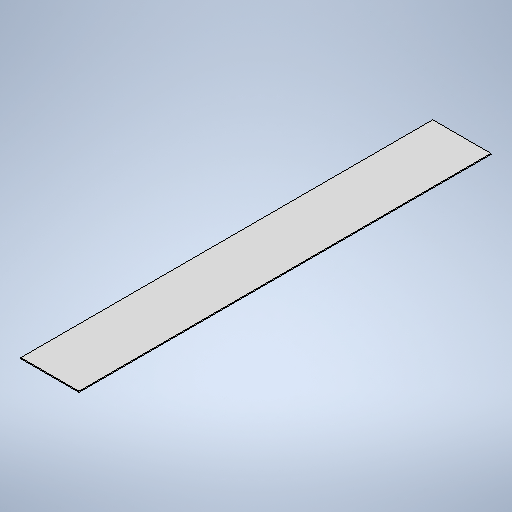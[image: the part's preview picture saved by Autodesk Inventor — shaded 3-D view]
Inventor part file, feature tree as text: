
AUTODESK INVENTOR PART (.ipt)
format: ipt  version: 2025 (Build 290162010, 162A)  size: 251,904 bytes
history: native  units: mm
features: sketch x2, sheet_metal_op x1, extrude x1, other x1
ambient origin geometry x8: Origin, YZ Plane, XZ Plane, XY Plane, X Axis, Y Axis, Z Axis, Center Point
bodies: Solid1 (feature_tree)
feature tree (5):
  sheet_metal_op  "Face1"
  extrude  "Extrusion1"  Depth=120.0mm
  sketch  "Sketch1"  dims[d0=120.0mm d1=850.054mm]
  other  "Plate1"
  sketch  "Sketch2"  dims[d2=2.0mm d4=2.443461mm d5=0.0mm d6=0.0mm]
